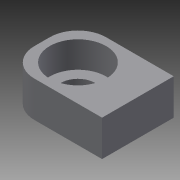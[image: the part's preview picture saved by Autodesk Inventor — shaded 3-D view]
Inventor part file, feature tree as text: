
AUTODESK INVENTOR PART (.ipt)
format: ipt  version: 2013 (Build 170138000, 138)  size: 100,864 bytes
history: native  units: in
note: dims shown in document units (in); Inventor stores cm internally (conversion verified against a paired STEP export)
features: extrude x3, sketch x3, fillet x1
ambient origin geometry x8: Origin, YZ Plane, XZ Plane, XY Plane, X Axis, Y Axis, Z Axis, Center Point
bodies: Solid1 (feature_tree)
feature tree (7):
  extrude  "Extrusion1"  Depth=1.5in
  extrude  "Extrusion2"  Depth=1.1811in
  extrude  "Extrusion3"  Depth=0.75in
  fillet  "Fillet1"  Radius=0.5512in
  sketch  "Sketch1"  dims[d0=2.005in d1=1.5in]
  sketch  "Sketch2"  dims[d2=0.75in d3=0.0in d4=1.1811in]
  sketch  "Sketch3"  dims[d5=0.75in d6=0.75in d7=0.5512in d8=0.0in d9=0.25in d10=0.2812in d11=0.0in d12=0.2328in d13=0.2328in d14=0.5906in d15=0.75in]
